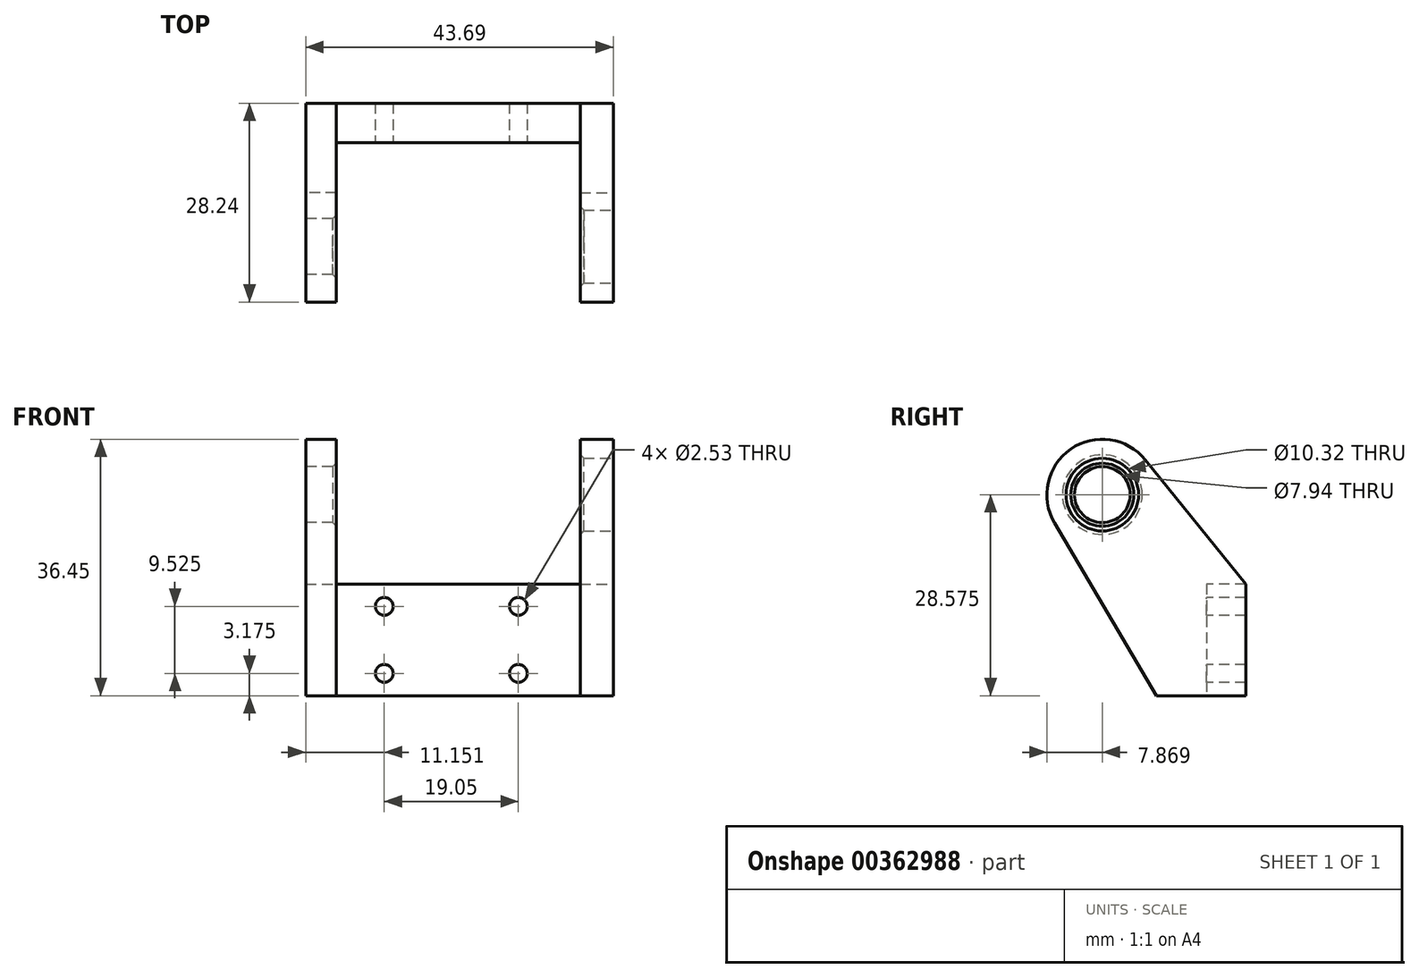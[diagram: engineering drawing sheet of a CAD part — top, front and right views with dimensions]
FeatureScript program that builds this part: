
annotation { "Feature Type Name" : "Feature", "Feature Type Description" : "" }
export const myFeature = defineFeature(function(context is Context, id is Id, definition is map)
    precondition{}
    {
        {
            var Q0;
            Q0=qCreatedBy(makeId("Front.planeOp"),FACE);
            var sketch = newSketch(context, id + "F0", { "sketchPlane" : qUnion([Q0])});
            skLineSegment(sketch, "E0.bottom", {"start": v(0, 0) * mm, "end": v(43.69, 0) * mm});
            skLineSegment(sketch, "E0.top", {"start": v(0, 15.88) * mm, "end": v(43.69, 15.88) * mm});
            skLineSegment(sketch, "E0.left", {"start": v(0, 0) * mm, "end": v(0, 15.88) * mm});
            skLineSegment(sketch, "E0.right", {"start": v(43.69, 0) * mm, "end": v(43.69, 15.88) * mm});
            skSolve(sketch);
        }
        {
            var Q0;
            Q0=makeQuery(id+"F0.imprint","IMPRINT",FACE,{"disambiguationData":[TD([[makeQuery(id+"F0.imprint","IMPRINT",EDGE,{"derivedFrom":sQuery(id+"F0.wireOp",EDGE,"E0.bottom")}),1.0]])]});
            extrude(context, id + "F1", {"entities" : qUnion([Q0]), "depth" : 5.6 * mm});
        }
        {
            var Q0;
            Q0=makeQuery(id+"F1.opExtrude","SWEPT_FACE",FACE,{"disambiguationData":[OSD([sQuery(id+"F0.wireOp",EDGE,"E0.right")])]});
            var sketch = newSketch(context, id + "F2", { "sketchPlane" : qUnion([Q0])});
            skCircle(sketch, "E1", {"center": v(-20.37, 28.57) * mm, "radius": 5.16 * mm});
            skLineSegment(sketch, "E2", {"start": v(0, 0) * mm, "end": v(-12.7, 0) * mm});
            skArc(sketch, "E3", {"start": v(-14.24, 33.52) * mm, "mid": v(-24.85, 35.05) * mm, "end": v(-27.16, 24.58) * mm});
            skLineSegment(sketch, "E4", {"start": v(-12.7, 0) * mm, "end": v(-27.16, 24.58) * mm});
            skLineSegment(sketch, "E5.0", {"start": v(0, 0) * mm, "end": v(0, 15.87) * mm});
            skLineSegment(sketch, "E6", {"start": v(0, 15.87) * mm, "end": v(-14.24, 33.52) * mm});
            skSolve(sketch);
        }
        {
            var Q0;
            Q0=makeQuery(id+"F2.imprint","IMPRINT",FACE,{"disambiguationData":[TD([[makeQuery(id+"F2.imprint","IMPRINT",EDGE,{"derivedFrom":sQuery(id+"F2.wireOp",EDGE,"E1")}),-1.0]])]});
            extrude(context, id + "F3", {"entities" : qUnion([Q0]), "operationType" : NewBodyOperationType.ADD, "oppositeDirection" : true, "depth" : 4.7 * mm});
        }
        {
            var Q0;
            Q0=makeQuery(id+"F1.opExtrude","SWEPT_FACE",FACE,{"disambiguationData":[OSD([sQuery(id+"F0.wireOp",EDGE,"E0.left")])]});
            var sketch = newSketch(context, id + "F4", { "sketchPlane" : qUnion([Q0])});
            skLineSegment(sketch, "E7.0.0", {"start": v(0, 15.88) * mm, "end": v(5.59, 15.88) * mm});
            skLineSegment(sketch, "E7.0.1", {"start": v(5.59, 15.88) * mm, "end": v(5.59, 0) * mm});
            skLineSegment(sketch, "E7.0.2", {"start": v(5.59, 0) * mm, "end": v(12.7, 0) * mm});
            skLineSegment(sketch, "E7.0.3", {"start": v(12.7, 0) * mm, "end": v(27.16, 24.58) * mm});
            skArc(sketch, "E7.0.4", {"start": v(27.16, 24.58) * mm, "mid": v(24.85, 35.05) * mm, "end": v(14.24, 33.52) * mm});
            skLineSegment(sketch, "E7.0.5", {"start": v(14.24, 33.52) * mm, "end": v(0, 15.88) * mm});
            skLineSegment(sketch, "E8.0", {"start": v(0, 0) * mm, "end": v(0, 15.88) * mm});
            skPoint(sketch, "E9.0", {"position": v(2.8, 0) * mm});
            skLineSegment(sketch, "E10.0", {"start": v(5.59, 0) * mm, "end": v(0, 0) * mm});
            skCircle(sketch, "E11", {"center": v(20.37, 28.58) * mm, "radius": 3.97 * mm});
            skSolve(sketch);
        }
        {
            var Q0;
            Q0 = qSketchRegion(id + "F4", true);
            extrude(context, id + "F5", {"entities" : qUnion([Q0]), "operationType" : NewBodyOperationType.ADD, "oppositeDirection" : true, "depth" : 4.32 * mm});
        }
        {
            var Q0;
            Q0=makeQuery(id+"F1.opExtrude","CAP_FACE",FACE,{"disambiguationData":[OSD([sQuery(id+"F0.wireOp",EDGE,"E0.bottom"),sQuery(id+"F0.wireOp",EDGE,"E0.top"),sQuery(id+"F0.wireOp",EDGE,"E0.left"),sQuery(id+"F0.wireOp",EDGE,"E0.right")])],"isStart":false});
            var sketch = newSketch(context, id + "F6", { "sketchPlane" : qUnion([Q0])});
            skPoint(sketch, "E12", {"position": v(11.15, 12.7) * mm});
            skPoint(sketch, "E13", {"position": v(30.2, 12.7) * mm});
            skPoint(sketch, "E14", {"position": v(30.2, 3.18) * mm});
            skPoint(sketch, "E15", {"position": v(11.15, 3.18) * mm});
            skSolve(sketch);
        }
        {
            var Q0;
            Q0=sQuery(id+"F6.wireOp",VERTEX,"E12");
            var Q1;
            Q1=sQuery(id+"F6.wireOp",VERTEX,"E13");
            var Q2;
            Q2=sQuery(id+"F6.wireOp",VERTEX,"E14");
            var Q3;
            Q3=sQuery(id+"F6.wireOp",VERTEX,"E15");
            var Q4;
            Q4=makeQuery(id+"F1.opExtrude","SWEPT_BODY",BODY,{"disambiguationData":[OSD([sQuery(id+"F0.wireOp",EDGE,"E0.bottom"),sQuery(id+"F0.wireOp",EDGE,"E0.top"),sQuery(id+"F0.wireOp",EDGE,"E0.left"),sQuery(id+"F0.wireOp",EDGE,"E0.right")])]});
            hole(context, id + "F7", {"style" : HoleStyle.SIMPLE, "endStyle" : HoleEndStyle.THROUGH, "standardTappedOrClearance" : lookupTablePath({ "standard" : "ANSI", "size" : "#39 (0.1)", "type" : "Drilled" }), "standardBlindInLast" : lookupTablePath({ "standard" : "ANSI", "size" : "#39", "type" : "Drilled" }), "holeDiameter" : 2.53 * mm, "tappedDepth" : 4.57 * mm, "tapClearance" : 3, "locations" : qUnion([Q0, Q1, Q2, Q3]), "scope" : qUnion([Q4])});
        }
        {
            var Q0;
            Q0=makeQuery(id+"F5.opExtrude","CAP_EDGE",EDGE,{"disambiguationData":[OSD([sQuery(id+"F4.wireOp",EDGE,"E11")])],"isStart":false});
            var Q1;
            Q1=makeQuery(id+"F3.opExtrude","CAP_EDGE",EDGE,{"disambiguationData":[OSD([sQuery(id+"F2.wireOp",EDGE,"E1")])],"isStart":false});
            chamfer(context, id + "F8", {"entities" : qUnion([Q0, Q1]), "width" : 0.5 * mm, "tangentPropagation" : true});
        }
    });
